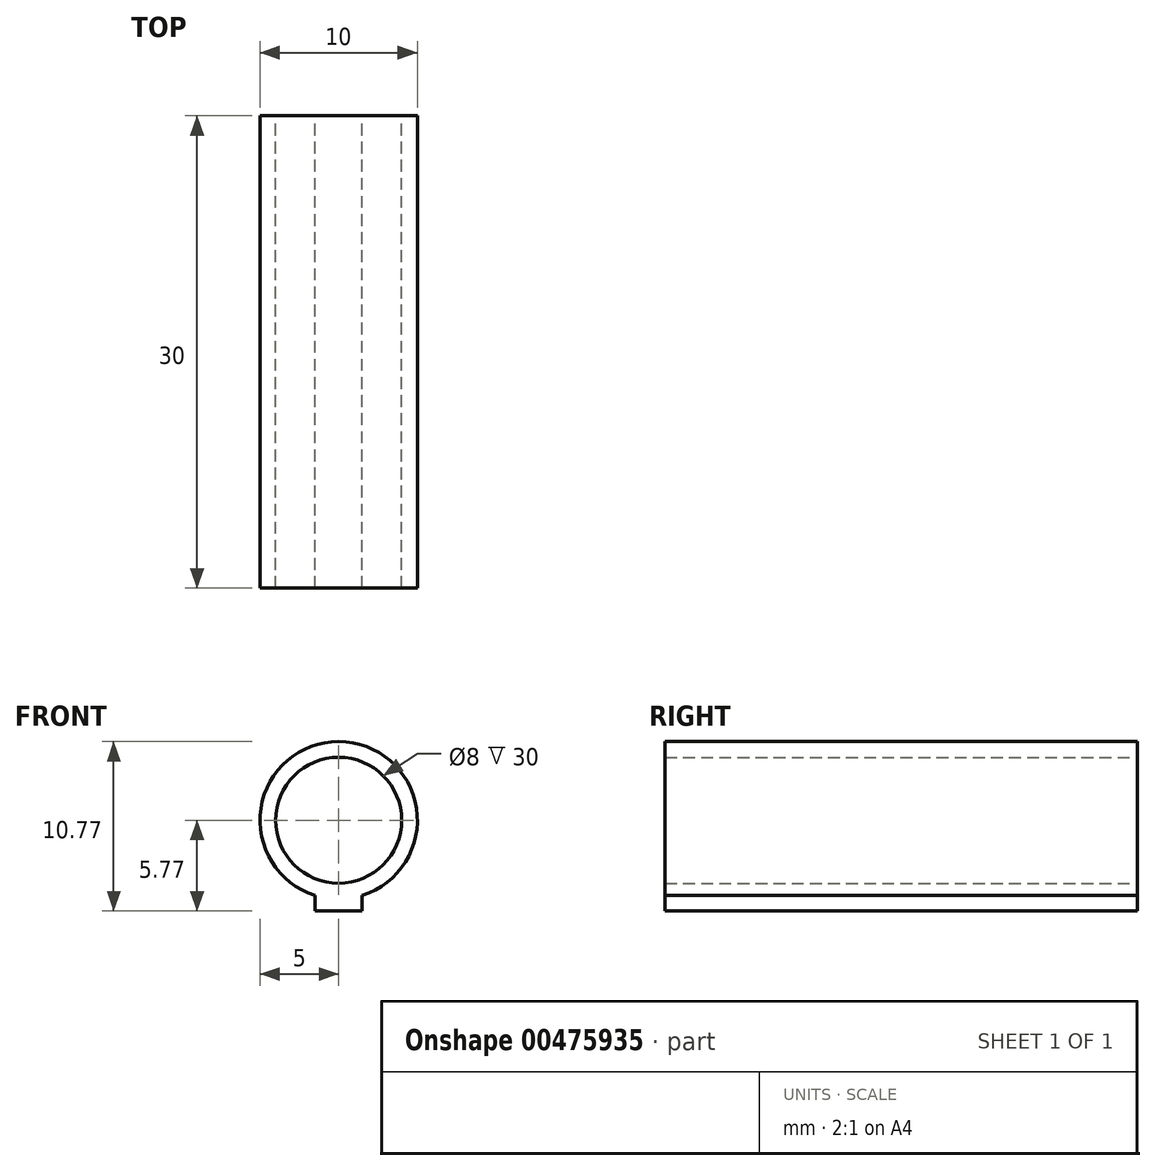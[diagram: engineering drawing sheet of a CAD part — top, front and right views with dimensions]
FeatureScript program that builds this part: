
annotation { "Feature Type Name" : "Feature", "Feature Type Description" : "" }
export const myFeature = defineFeature(function(context is Context, id is Id, definition is map)
    precondition{}
    {
        {
            var Q0;
            Q0=qCreatedBy(makeId("Front.planeOp"),FACE);
            var sketch = newSketch(context, id + "F0", { "sketchPlane" : qUnion([Q0])});
            skArc(sketch, "E0", {"start": v(1.5, -4.77) * mm, "mid": v(0, 5) * mm, "end": v(-1.5, -4.77) * mm});
            skCircle(sketch, "E1", {"center": v(0, 0) * mm, "radius": 4 * mm});
            skLineSegment(sketch, "E2.top", {"start": v(-1.5, -5.77) * mm, "end": v(1.5, -5.77) * mm});
            skLineSegment(sketch, "E2.left", {"start": v(-1.5, -4.77) * mm, "end": v(-1.5, -5.77) * mm});
            skLineSegment(sketch, "E2.right", {"start": v(1.5, -4.77) * mm, "end": v(1.5, -5.77) * mm});
            skSolve(sketch);
        }
        {
            var Q0;
            Q0=makeQuery(id+"F0.imprint","IMPRINT",FACE,{"disambiguationData":[TD([[makeQuery(id+"F0.imprint","IMPRINT",EDGE,{"derivedFrom":sQuery(id+"F0.wireOp",EDGE,"E0")}),1.0]])]});
            extrude(context, id + "F1", {"entities" : qUnion([Q0]), "endBound" : BoundingType.SYMMETRIC, "depth" : 30 * mm});
        }
    });
